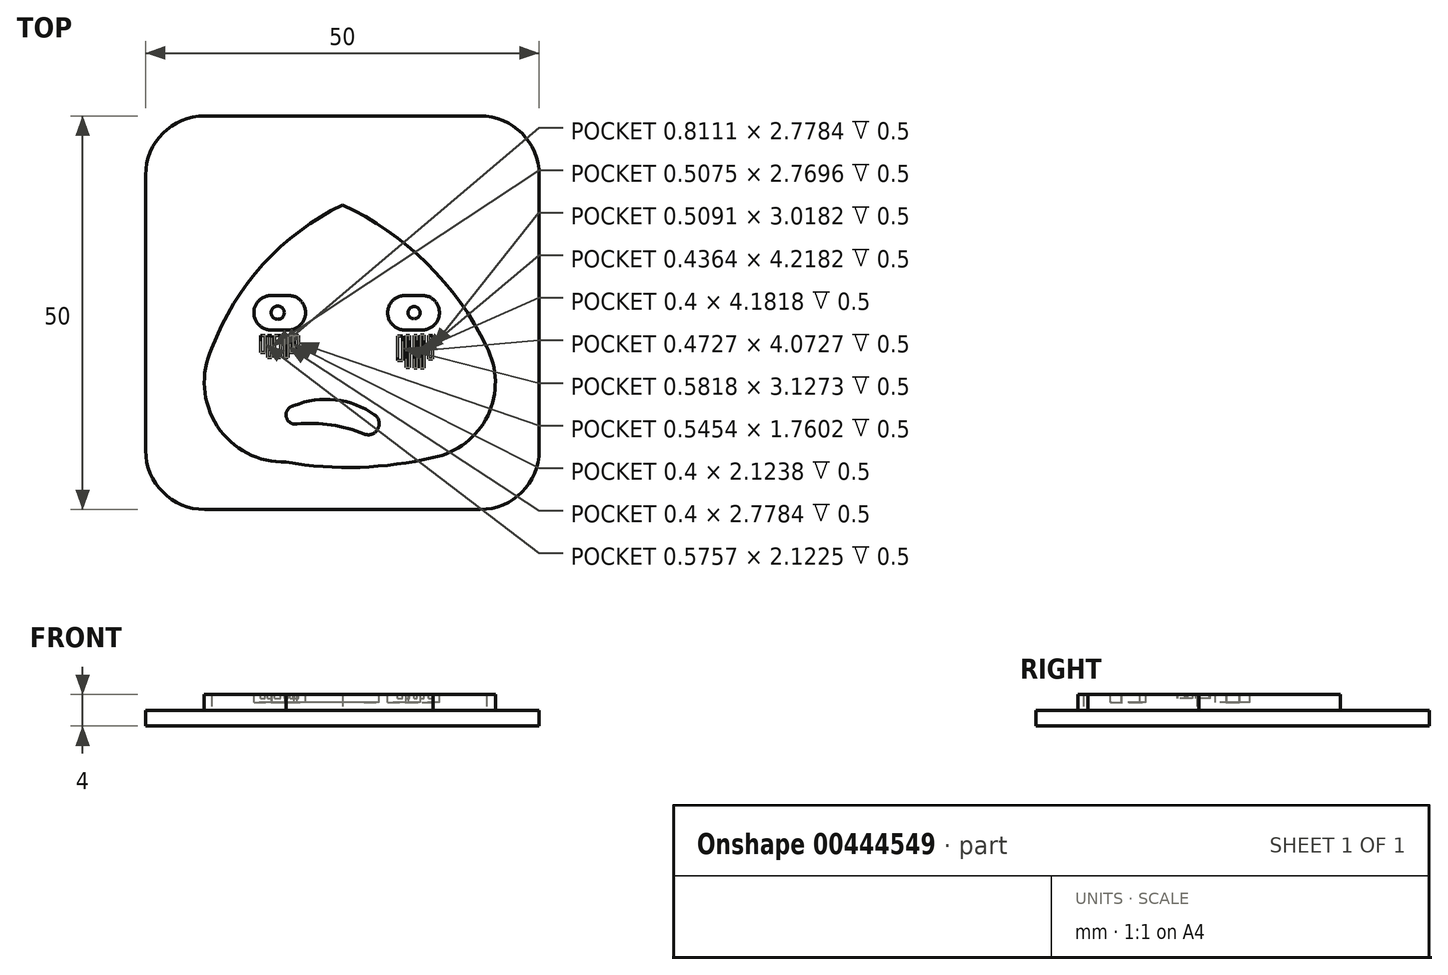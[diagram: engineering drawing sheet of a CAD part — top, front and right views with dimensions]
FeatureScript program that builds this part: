
annotation { "Feature Type Name" : "Feature", "Feature Type Description" : "" }
export const myFeature = defineFeature(function(context is Context, id is Id, definition is map)
    precondition{}
    {
        {
            var Q0;
            Q0=qCreatedBy(makeId("Top.planeOp"),FACE);
            var sketch = newSketch(context, id + "F0", { "sketchPlane" : qUnion([Q0])});
            skLineSegment(sketch, "E0.bottom", {"start": v(-17.5, 25) * mm, "end": v(17.5, 25) * mm});
            skLineSegment(sketch, "E0.top", {"start": v(-17.5, -25) * mm, "end": v(17.5, -25) * mm});
            skLineSegment(sketch, "E0.left", {"start": v(-25, 17.5) * mm, "end": v(-25, -17.5) * mm});
            skLineSegment(sketch, "E0.right", {"start": v(25, 17.5) * mm, "end": v(25, -17.5) * mm});
            skPoint(sketch, "E0.middle", {"position": v(0, 0) * mm});
            skPoint(sketch, "E1.visualSharp", {"position": v(-25, 25) * mm});
            skArc(sketch, "E1.filletArc", {"start": v(-17.5, 25) * mm, "mid": v(-22.8, 22.8) * mm, "end": v(-25, 17.5) * mm});
            skPoint(sketch, "E2.visualSharp", {"position": v(25, 25) * mm});
            skArc(sketch, "E2.filletArc", {"start": v(25, 17.5) * mm, "mid": v(22.8, 22.8) * mm, "end": v(17.5, 25) * mm});
            skPoint(sketch, "E3.visualSharp", {"position": v(25, -25) * mm});
            skArc(sketch, "E3.filletArc", {"start": v(17.5, -25) * mm, "mid": v(22.8, -22.8) * mm, "end": v(25, -17.5) * mm});
            skPoint(sketch, "E4.visualSharp", {"position": v(-25, -25) * mm});
            skArc(sketch, "E4.filletArc", {"start": v(-25, -17.5) * mm, "mid": v(-22.8, -22.8) * mm, "end": v(-17.5, -25) * mm});
            skSolve(sketch);
        }
        {
            var Q0;
            Q0 = qSketchRegion(id + "F0", true);
            extrude(context, id + "F1", {"entities" : qUnion([Q0]), "depth" : 2 * mm});
        }
        {
            var Q0;
            Q0=makeQuery(id+"F1.opExtrude","CAP_FACE",FACE,{"disambiguationData":[OSD([sQuery(id+"F0.wireOp",EDGE,"E0.bottom"),sQuery(id+"F0.wireOp",EDGE,"E0.top"),sQuery(id+"F0.wireOp",EDGE,"E0.left"),sQuery(id+"F0.wireOp",EDGE,"E0.right"),sQuery(id+"F0.wireOp",EDGE,"E1.filletArc"),sQuery(id+"F0.wireOp",EDGE,"E2.filletArc"),sQuery(id+"F0.wireOp",EDGE,"E3.filletArc"),sQuery(id+"F0.wireOp",EDGE,"E4.filletArc")])],"isStart":false});
            var sketch = newSketch(context, id + "F2", { "sketchPlane" : qUnion([Q0])});
            skArc(sketch, "E5", {"start": v(-16.6, -4.55) * mm, "mid": v(-15.9, -14.4) * mm, "end": v(-7.15, -18.98) * mm});
            skArc(sketch, "E6", {"start": v(11.51, -18.4) * mm, "mid": v(18.46, -13.06) * mm, "end": v(18.29, -4.3) * mm});
            skArc(sketch, "E7", {"start": v(-7.15, -18.98) * mm, "mid": v(2.21, -19.63) * mm, "end": v(11.51, -18.4) * mm});
            skArc(sketch, "E8", {"start": v(0, 13.7) * mm, "mid": v(-10.82, 5.3) * mm, "end": v(-17.34, -6.77) * mm});
            skArc(sketch, "E9", {"start": v(18.71, -5.22) * mm, "mid": v(11.06, 5.93) * mm, "end": v(0, 13.7) * mm});
            skSolve(sketch);
        }
        {
            var Q0;
            Q0 = qSketchRegion(id + "F2", true);
            extrude(context, id + "F3", {"entities" : qUnion([Q0]), "operationType" : NewBodyOperationType.ADD, "depth" : 2 * mm});
        }
        {
            var Q0;
            Q0=makeQuery(id+"F3.opExtrude","CAP_FACE",FACE,{"disambiguationData":[OSD([sQuery(id+"F2.wireOp",EDGE,"E5"),sQuery(id+"F2.wireOp",EDGE,"E6"),sQuery(id+"F2.wireOp",EDGE,"E7"),sQuery(id+"F2.wireOp",EDGE,"E8"),sQuery(id+"F2.wireOp",EDGE,"E9")])],"isStart":false});
            var sketch = newSketch(context, id + "F4", { "sketchPlane" : qUnion([Q0])});
            skArc(sketch, "E10", {"start": v(-9.06, 2.2) * mm, "mid": v(-11.25, -0.07) * mm, "end": v(-8.93, -2.19) * mm});
            skArc(sketch, "E11", {"start": v(-6.88, -2.2) * mm, "mid": v(-4.68, 0) * mm, "end": v(-6.87, 2.2) * mm});
            skLineSegment(sketch, "E12", {"start": v(-9.06, 2.2) * mm, "end": v(-6.87, 2.2) * mm});
            skLineSegment(sketch, "E13", {"start": v(-9.21, -2.19) * mm, "end": v(-6.88, -2.2) * mm});
            skLineSegment(sketch, "E14.1.0.0", {"start": v(7.94, 2.2) * mm, "end": v(10.13, 2.2) * mm});
            skArc(sketch, "E14.1.0.1", {"start": v(10.12, -2.2) * mm, "mid": v(12.32, 0) * mm, "end": v(10.13, 2.2) * mm});
            skArc(sketch, "E14.1.0.2", {"start": v(7.94, 2.2) * mm, "mid": v(5.75, -0.07) * mm, "end": v(8.07, -2.19) * mm});
            skLineSegment(sketch, "E14.1.0.3", {"start": v(7.79, -2.19) * mm, "end": v(10.12, -2.2) * mm});
            skLineSegment(sketch, "E14.direction1", {"start": v(-9.06, 2.2) * mm, "end": v(7.94, 2.2) * mm, "construction": true});
            skArc(sketch, "E15", {"start": v(-6.15, -11.81) * mm, "mid": v(-7.15, -13.17) * mm, "end": v(-5.77, -14.13) * mm});
            skArc(sketch, "E16", {"start": v(2.75, -15.4) * mm, "mid": v(4.5, -14.79) * mm, "end": v(4.09, -12.98) * mm});
            skArc(sketch, "E17", {"start": v(4.09, -12.98) * mm, "mid": v(-1.22, -11.03) * mm, "end": v(-6.77, -12.1) * mm});
            skArc(sketch, "E18", {"start": v(2.75, -15.4) * mm, "mid": v(-1.55, -14.25) * mm, "end": v(-6, -14.15) * mm});
            skSolve(sketch);
        }
        {
            var Q0;
            Q0 = qSketchRegion(id + "F4", true);
            extrude(context, id + "F5", {"entities" : qUnion([Q0]), "operationType" : NewBodyOperationType.REMOVE, "oppositeDirection" : true, "depth" : 1 * mm});
        }
        {
            var Q0;
            Q0=makeQuery(id+"F5.boolean.opBoolean","COPY",FACE,{"derivedFrom":makeQuery(id+"F5.opExtrude","CAP_FACE",FACE,{"disambiguationData":[OSD([sQuery(id+"F4.wireOp",EDGE,"E10"),sQuery(id+"F4.wireOp",EDGE,"E11"),sQuery(id+"F4.wireOp",EDGE,"E12"),sQuery(id+"F4.wireOp",EDGE,"E13")])],"isStart":false})});
            var sketch = newSketch(context, id + "F6", { "sketchPlane" : qUnion([Q0])});
            skCircle(sketch, "E19", {"center": v(-8.22, 0) * mm, "radius": 0.84 * mm});
            skSolve(sketch);
        }
        {
            var Q0;
            Q0 = qSketchRegion(id + "F6", true);
            extrude(context, id + "F7", {"entities" : qUnion([Q0]), "operationType" : NewBodyOperationType.ADD, "depth" : 1 * mm});
        }
        {
            var Q0;
            Q0=makeQuery(id+"F5.boolean.opBoolean","COPY",FACE,{"derivedFrom":makeQuery(id+"F5.opExtrude","CAP_FACE",FACE,{"disambiguationData":[OSD([sQuery(id+"F4.wireOp",EDGE,"E14.1.0.0"),sQuery(id+"F4.wireOp",EDGE,"E14.1.0.1"),sQuery(id+"F4.wireOp",EDGE,"E14.1.0.2"),sQuery(id+"F4.wireOp",EDGE,"E14.1.0.3")])],"isStart":false})});
            var sketch = newSketch(context, id + "F8", { "sketchPlane" : qUnion([Q0])});
            skCircle(sketch, "E20", {"center": v(9.1, 0) * mm, "radius": 0.77 * mm});
            skSolve(sketch);
        }
        {
            var Q0;
            Q0 = qSketchRegion(id + "F8", true);
            extrude(context, id + "F9", {"entities" : qUnion([Q0]), "operationType" : NewBodyOperationType.ADD, "depth" : 1 * mm});
        }
        {
            var Q0;
            Q0=makeQuery(id+"F3.opExtrude","CAP_FACE",FACE,{"disambiguationData":[OSD([sQuery(id+"F2.wireOp",EDGE,"E5"),sQuery(id+"F2.wireOp",EDGE,"E6"),sQuery(id+"F2.wireOp",EDGE,"E7"),sQuery(id+"F2.wireOp",EDGE,"E8"),sQuery(id+"F2.wireOp",EDGE,"E9")])],"isStart":false});
            var sketch = newSketch(context, id + "F10", { "sketchPlane" : qUnion([Q0])});
            skLineSegment(sketch, "E21.bottom", {"start": v(-10.42, -2.92) * mm, "end": v(-9.85, -2.92) * mm});
            skLineSegment(sketch, "E21.top", {"start": v(-10.42, -5.05) * mm, "end": v(-9.85, -5.05) * mm});
            skLineSegment(sketch, "E21.left", {"start": v(-10.42, -2.92) * mm, "end": v(-10.42, -5.05) * mm});
            skLineSegment(sketch, "E21.right", {"start": v(-9.85, -2.92) * mm, "end": v(-9.85, -5.05) * mm});
            skLineSegment(sketch, "E22.bottom", {"start": v(-7.33, -2.92) * mm, "end": v(-6.93, -2.92) * mm});
            skLineSegment(sketch, "E22.top", {"start": v(-7.33, -5.7) * mm, "end": v(-6.93, -5.7) * mm});
            skLineSegment(sketch, "E22.left", {"start": v(-7.33, -2.92) * mm, "end": v(-7.33, -5.7) * mm});
            skLineSegment(sketch, "E22.right", {"start": v(-6.93, -2.92) * mm, "end": v(-6.93, -5.7) * mm});
            skLineSegment(sketch, "E23.bottom", {"start": v(-6.67, -2.92) * mm, "end": v(-6.27, -2.92) * mm});
            skLineSegment(sketch, "E23.top", {"start": v(-6.67, -5.05) * mm, "end": v(-6.27, -5.05) * mm});
            skLineSegment(sketch, "E23.left", {"start": v(-6.67, -2.92) * mm, "end": v(-6.67, -5.05) * mm});
            skLineSegment(sketch, "E23.right", {"start": v(-6.27, -2.92) * mm, "end": v(-6.27, -5.05) * mm});
            skLineSegment(sketch, "E24.bottom", {"start": v(-6.1, -2.92) * mm, "end": v(-5.55, -2.92) * mm});
            skLineSegment(sketch, "E24.top", {"start": v(-6.1, -4.68) * mm, "end": v(-5.55, -4.68) * mm});
            skLineSegment(sketch, "E24.left", {"start": v(-6.1, -2.92) * mm, "end": v(-6.1, -4.68) * mm});
            skLineSegment(sketch, "E24.right", {"start": v(-5.55, -2.92) * mm, "end": v(-5.55, -4.68) * mm});
            skLineSegment(sketch, "E25.bottom", {"start": v(7.03, -2.94) * mm, "end": v(7.6, -2.94) * mm});
            skLineSegment(sketch, "E25.top", {"start": v(7.03, -6.07) * mm, "end": v(7.6, -6.07) * mm});
            skLineSegment(sketch, "E25.left", {"start": v(7.03, -2.94) * mm, "end": v(7.03, -6.07) * mm});
            skLineSegment(sketch, "E25.right", {"start": v(7.6, -2.94) * mm, "end": v(7.6, -6.07) * mm});
            skLineSegment(sketch, "E26.bottom", {"start": v(8.08, -2.9) * mm, "end": v(8.55, -2.9) * mm});
            skLineSegment(sketch, "E26.top", {"start": v(8.08, -6.98) * mm, "end": v(8.55, -6.98) * mm});
            skLineSegment(sketch, "E26.left", {"start": v(8.08, -2.9) * mm, "end": v(8.08, -6.98) * mm});
            skLineSegment(sketch, "E26.right", {"start": v(8.55, -2.9) * mm, "end": v(8.55, -6.98) * mm});
            skLineSegment(sketch, "E27.bottom", {"start": v(9.06, -2.87) * mm, "end": v(9.46, -2.87) * mm});
            skLineSegment(sketch, "E27.top", {"start": v(9.06, -7.05) * mm, "end": v(9.46, -7.05) * mm});
            skLineSegment(sketch, "E27.left", {"start": v(9.06, -2.87) * mm, "end": v(9.06, -7.05) * mm});
            skLineSegment(sketch, "E27.right", {"start": v(9.46, -2.87) * mm, "end": v(9.46, -7.05) * mm});
            skLineSegment(sketch, "E28.bottom", {"start": v(9.94, -2.83) * mm, "end": v(10.37, -2.83) * mm});
            skLineSegment(sketch, "E28.top", {"start": v(9.94, -7.05) * mm, "end": v(10.37, -7.05) * mm});
            skLineSegment(sketch, "E28.left", {"start": v(9.94, -2.83) * mm, "end": v(9.94, -7.05) * mm});
            skLineSegment(sketch, "E28.right", {"start": v(10.37, -2.83) * mm, "end": v(10.37, -7.05) * mm});
            skLineSegment(sketch, "E29.bottom", {"start": v(10.95, -2.87) * mm, "end": v(11.46, -2.87) * mm});
            skLineSegment(sketch, "E29.top", {"start": v(10.95, -5.88) * mm, "end": v(11.46, -5.88) * mm});
            skLineSegment(sketch, "E29.left", {"start": v(10.95, -2.87) * mm, "end": v(10.95, -5.88) * mm});
            skLineSegment(sketch, "E29.right", {"start": v(11.46, -2.87) * mm, "end": v(11.46, -5.88) * mm});
            skLineSegment(sketch, "E30.bottom", {"start": v(-9.5, -2.92) * mm, "end": v(-8.99, -2.92) * mm});
            skLineSegment(sketch, "E30.top", {"start": v(-9.5, -5.7) * mm, "end": v(-8.99, -5.7) * mm});
            skLineSegment(sketch, "E30.left", {"start": v(-9.5, -2.92) * mm, "end": v(-9.5, -5.7) * mm});
            skLineSegment(sketch, "E30.right", {"start": v(-8.99, -2.92) * mm, "end": v(-8.99, -5.7) * mm});
            skLineSegment(sketch, "E31.bottom", {"start": v(-8.65, -2.92) * mm, "end": v(-7.83, -2.92) * mm});
            skLineSegment(sketch, "E31.top", {"start": v(-8.65, -5.7) * mm, "end": v(-7.83, -5.7) * mm});
            skLineSegment(sketch, "E31.left", {"start": v(-8.65, -2.92) * mm, "end": v(-8.65, -5.7) * mm});
            skLineSegment(sketch, "E31.right", {"start": v(-7.83, -2.92) * mm, "end": v(-7.83, -5.7) * mm});
            skSolve(sketch);
        }
        {
            var Q0;
            Q0 = qSketchRegion(id + "F10", true);
            extrude(context, id + "F11", {"entities" : qUnion([Q0]), "operationType" : NewBodyOperationType.REMOVE, "oppositeDirection" : true, "depth" : 0.5 * mm});
        }
    });
